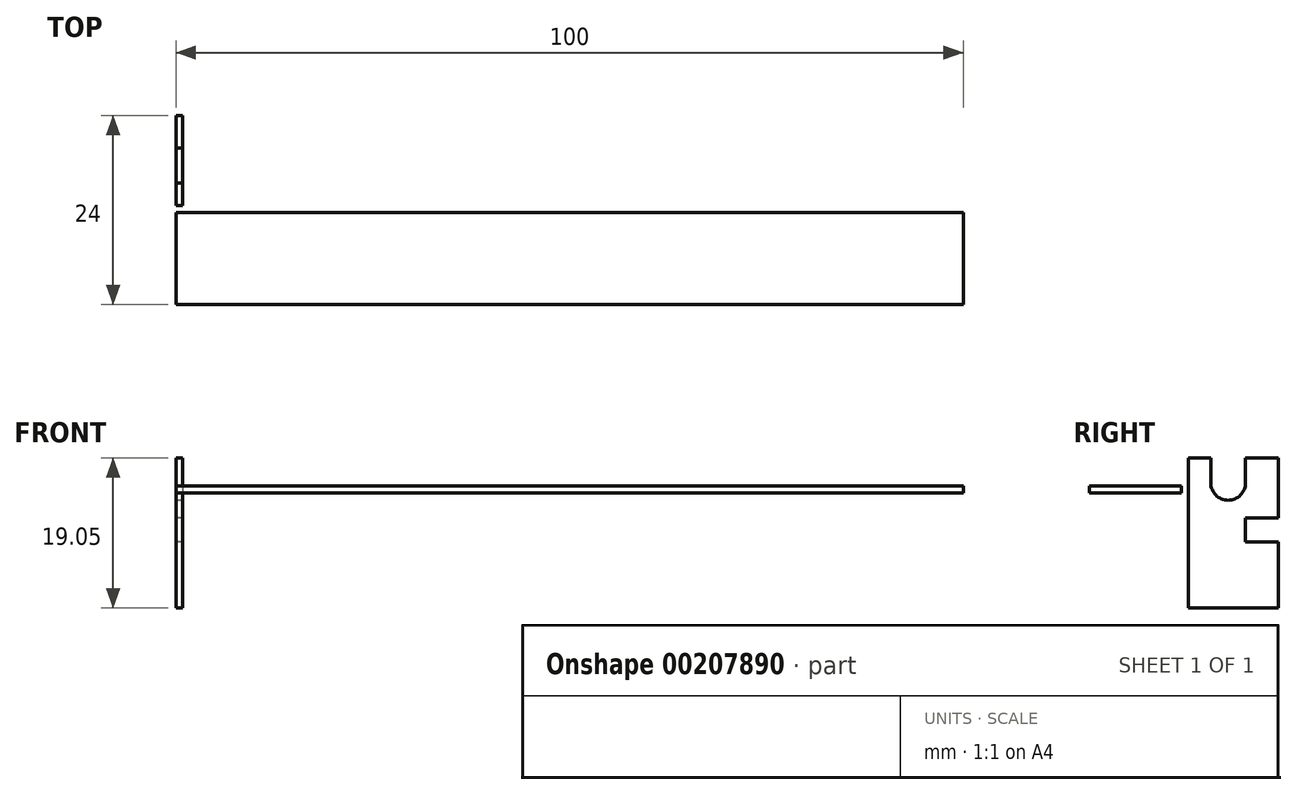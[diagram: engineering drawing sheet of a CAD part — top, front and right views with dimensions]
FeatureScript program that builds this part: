
annotation { "Feature Type Name" : "Feature", "Feature Type Description" : "" }
export const myFeature = defineFeature(function(context is Context, id is Id, definition is map)
    precondition{}
    {
        {
            var Q0;
            Q0=qCreatedBy(makeId("Top.planeOp"),FACE);
            var sketch = newSketch(context, id + "F0", { "sketchPlane" : qUnion([Q0])});
            skLineSegment(sketch, "E0.bottom", {"start": v(-143.4, -300) * mm, "end": v(-114.55, -300) * mm});
            skLineSegment(sketch, "E0.top", {"start": v(-143.4, 0) * mm, "end": v(-114.55, 0) * mm});
            skLineSegment(sketch, "E0.left", {"start": v(-143.4, -300) * mm, "end": v(-143.4, 0) * mm});
            skLineSegment(sketch, "E0.right", {"start": v(-114.55, -300) * mm, "end": v(-114.55, 0) * mm});
            skPoint(sketch, "E1", {"position": v(-3.4, -300) * mm});
            skLineSegment(sketch, "E2", {"start": v(11.76, 1.03) * mm, "end": v(11.76, 1.89) * mm});
            skLineSegment(sketch, "E3", {"start": v(11.76, 1.89) * mm, "end": v(-108.26, 1.89) * mm});
            skLineSegment(sketch, "E4", {"start": v(-108.26, 1.89) * mm, "end": v(-108.26, 13.32) * mm});
            skLineSegment(sketch, "E5", {"start": v(-108.26, 13.32) * mm, "end": v(-109.12, 13.32) * mm});
            skLineSegment(sketch, "E6.bottom", {"start": v(-114.55, -300) * mm, "end": v(-16.15, -300) * mm});
            skLineSegment(sketch, "E6.top", {"start": v(-114.55, 0) * mm, "end": v(-16.15, 0) * mm});
            skLineSegment(sketch, "E6.right", {"start": v(-16.15, -300) * mm, "end": v(-16.15, 0) * mm});
            skLineSegment(sketch, "E7.bottom", {"start": v(-16.15, 0) * mm, "end": v(-7.9, 0) * mm});
            skLineSegment(sketch, "E7.top", {"start": v(-16.15, -15) * mm, "end": v(-7.9, -15) * mm});
            skLineSegment(sketch, "E7.left", {"start": v(-16.15, 0) * mm, "end": v(-16.15, -15) * mm});
            skLineSegment(sketch, "E7.right", {"start": v(-7.9, 0) * mm, "end": v(-7.9, -15) * mm});
            skPoint(sketch, "E8", {"position": v(-7.9, -300) * mm});
            skLineSegment(sketch, "E9.bottom", {"start": v(-16.15, -33.36) * mm, "end": v(-7.9, -33.36) * mm});
            skLineSegment(sketch, "E9.top", {"start": v(-16.15, -41.36) * mm, "end": v(-7.9, -41.36) * mm});
            skLineSegment(sketch, "E9.left", {"start": v(-16.15, -33.36) * mm, "end": v(-16.15, -41.36) * mm});
            skLineSegment(sketch, "E9.right", {"start": v(-7.9, -33.36) * mm, "end": v(-7.9, -41.36) * mm});
            skPoint(sketch, "E10", {"position": v(-3.4, 0) * mm});
            skLineSegment(sketch, "E11", {"start": v(-16.15, -45.01) * mm, "end": v(-3.4, -45.01) * mm});
            skLineSegment(sketch, "E12", {"start": v(-3.4, -45.01) * mm, "end": v(-3.4, -56.21) * mm});
            skLineSegment(sketch, "E13", {"start": v(-3.4, -56.21) * mm, "end": v(-11.8, -56.21) * mm});
            skLineSegment(sketch, "E14", {"start": v(-11.8, -56.21) * mm, "end": v(-11.8, -58.11) * mm});
            skLineSegment(sketch, "E15", {"start": v(-11.8, -58.11) * mm, "end": v(-3.4, -58.11) * mm});
            skLineSegment(sketch, "E16", {"start": v(-3.4, -58.11) * mm, "end": v(-3.4, -129.31) * mm});
            skLineSegment(sketch, "E17", {"start": v(-3.4, -129.31) * mm, "end": v(-16.15, -129.31) * mm});
            skPoint(sketch, "E18", {"position": v(-11.8, -57.16) * mm});
            skArc(sketch, "E19", {"start": v(-14.33, -41.36) * mm, "mid": v(-16.15, -43.19) * mm, "end": v(-14.33, -45.01) * mm});
            skArc(sketch, "E20", {"start": v(-10.85, -56.21) * mm, "mid": v(-11.8, -57.16) * mm, "end": v(-10.85, -58.11) * mm});
            skLineSegment(sketch, "E21", {"start": v(-16.15, -139.06) * mm, "end": v(-11.35, -139.06) * mm});
            skLineSegment(sketch, "E22", {"start": v(-11.35, -139.06) * mm, "end": v(-11.35, -144.76) * mm});
            skLineSegment(sketch, "E23", {"start": v(-11.35, -144.76) * mm, "end": v(-8.77, -144.76) * mm});
            skLineSegment(sketch, "E24", {"start": v(-8.77, -144.76) * mm, "end": v(-6.35, -143.36) * mm});
            skLineSegment(sketch, "E25", {"start": v(-6.35, -143.36) * mm, "end": v(-6.35, -132.06) * mm});
            skLineSegment(sketch, "E26", {"start": v(-6.35, -132.06) * mm, "end": v(-12.38, -132.06) * mm});
            skLineSegment(sketch, "E27", {"start": v(-12.38, -132.06) * mm, "end": v(-12.38, -129.31) * mm});
            skArc(sketch, "E28", {"start": v(-11, -129.31) * mm, "mid": v(-12.38, -130.69) * mm, "end": v(-11, -132.06) * mm});
            skLineSegment(sketch, "E29", {"start": v(-108.26, 1.89) * mm, "end": v(-109.12, 1.89) * mm});
            skLineSegment(sketch, "E30", {"start": v(-109.12, 13.32) * mm, "end": v(-109.12, 1.89) * mm});
            skLineSegment(sketch, "E31", {"start": v(-109.12, 1.03) * mm, "end": v(-109.12, 1.89) * mm});
            skLineSegment(sketch, "E32", {"start": v(-108.26, 1.89) * mm, "end": v(-108.26, 1.03) * mm});
            skLineSegment(sketch, "E33", {"start": v(-108.26, 1.03) * mm, "end": v(-109.12, 1.03) * mm});
            skLineSegment(sketch, "E34", {"start": v(-108.26, 1.03) * mm, "end": v(11.76, 1.03) * mm});
            skPoint(sketch, "E35", {"position": v(0, -57.16) * mm});
            skSolve(sketch);
        }
        {
            var Q0;
            {var subQ7=sQuery(id+"F0.wireOp",EDGE,"E6.bottom");Q0=makeQuery(id+"F0.imprint","IMPRINT",FACE,{"disambiguationData":[TD([[makeQuery(id+"F0.imprint","IMPRINT",EDGE,{"derivedFrom":subQ7}),1.0]])]});}
            var Q1;
            {var subQ5=sQuery(id+"F0.wireOp",EDGE,"E21");Q1=makeQuery(id+"F0.imprint","IMPRINT",FACE,{"disambiguationData":[TD([[makeQuery(id+"F0.imprint","IMPRINT",EDGE,{"derivedFrom":subQ5}),1.0]])]});}
            var Q2;
            {var subQ0=sQuery(id+"F0.wireOp",EDGE,"E27");var subQ1=sQuery(id+"F0.wireOp",EDGE,"E26");var subQ2=makeQuery(id+"F0.imprint","INTERSECT",VERTEX,{"derivedFrom":[subQ1,subQ0]});Q2=makeQuery(id+"F0.imprint","IMPRINT",FACE,{"disambiguationData":[TD([[makeQuery(id+"F0.imprint","IMPRINT",EDGE,{"disambiguationData":[TD([[subQ2,1.0]])],"derivedFrom":subQ1}),-1.0]])]});}
            var Q3;
            {var subQ0=sQuery(id+"F0.wireOp",EDGE,"E27");var subQ1=sQuery(id+"F0.wireOp",EDGE,"E17");var subQ2=makeQuery(id+"F0.imprint","INTERSECT",VERTEX,{"derivedFrom":[subQ1,subQ0]});Q3=makeQuery(id+"F0.imprint","IMPRINT",FACE,{"disambiguationData":[TD([[makeQuery(id+"F0.imprint","IMPRINT",EDGE,{"disambiguationData":[TD([[subQ2,1.0]])],"derivedFrom":subQ1}),1.0]])]});}
            var Q4;
            {var subQ0=sQuery(id+"F0.wireOp",EDGE,"E15");var subQ1=sQuery(id+"F0.wireOp",EDGE,"E14");var subQ2=makeQuery(id+"F0.imprint","INTERSECT",VERTEX,{"derivedFrom":[subQ1,subQ0]});Q4=makeQuery(id+"F0.imprint","IMPRINT",FACE,{"disambiguationData":[TD([[makeQuery(id+"F0.imprint","IMPRINT",EDGE,{"disambiguationData":[TD([[subQ2,1.0]])],"derivedFrom":subQ1}),1.0]])]});}
            var Q5;
            {var subQ0=sQuery(id+"F0.wireOp",EDGE,"E14");var subQ1=sQuery(id+"F0.wireOp",EDGE,"E13");var subQ2=makeQuery(id+"F0.imprint","INTERSECT",VERTEX,{"derivedFrom":[subQ1,subQ0]});Q5=makeQuery(id+"F0.imprint","IMPRINT",FACE,{"disambiguationData":[TD([[makeQuery(id+"F0.imprint","IMPRINT",EDGE,{"disambiguationData":[TD([[subQ2,1.0]])],"derivedFrom":subQ1}),1.0]])]});}
            var Q6;
            {var subQ4=sQuery(id+"F0.wireOp",EDGE,"E12");Q6=makeQuery(id+"F0.imprint","IMPRINT",FACE,{"disambiguationData":[TD([[makeQuery(id+"F0.imprint","IMPRINT",EDGE,{"derivedFrom":subQ4}),-1.0]])]});}
            var Q7;
            {var subQ0=sQuery(id+"F0.wireOp",EDGE,"E11");var subQ1=sQuery(id+"F0.wireOp",EDGE,"E6.right");var subQ2=makeQuery(id+"F0.imprint","INTERSECT",VERTEX,{"derivedFrom":[subQ1,subQ0]});Q7=makeQuery(id+"F0.imprint","IMPRINT",FACE,{"disambiguationData":[TD([[makeQuery(id+"F0.imprint","IMPRINT",EDGE,{"disambiguationData":[TD([[subQ2,-1.0]])],"derivedFrom":subQ1}),-1.0]])]});}
            var Q8;
            {var subQ0=sQuery(id+"F0.wireOp",EDGE,"E9.top");var subQ3=sQuery(id+"F0.wireOp",EDGE,"E19");var subQ5=makeQuery(id+"F0.imprint","INTERSECT",VERTEX,{"derivedFrom":[subQ0,subQ3]});Q8=makeQuery(id+"F0.imprint","IMPRINT",FACE,{"disambiguationData":[TD([[makeQuery(id+"F0.imprint","IMPRINT",EDGE,{"disambiguationData":[TD([[subQ5,-1.0]])],"derivedFrom":subQ3}),-1.0]])]});}
            var Q9;
            Q9=makeQuery(id+"F0.imprint","IMPRINT",FACE,{"disambiguationData":[TD([[makeQuery(id+"F0.imprint","IMPRINT",EDGE,{"derivedFrom":sQuery(id+"F0.wireOp",EDGE,"E9.bottom")}),-1.0]])]});
            var Q10;
            Q10=makeQuery(id+"F0.imprint","IMPRINT",FACE,{"disambiguationData":[TD([[makeQuery(id+"F0.imprint","IMPRINT",EDGE,{"derivedFrom":sQuery(id+"F0.wireOp",EDGE,"E7.bottom")}),-1.0]])]});
            extrude(context, id + "F1", {"entities" : qUnion([Q0, Q1, Q2, Q3, Q4, Q5, Q6, Q7, Q8, Q9, Q10]), "endBound" : BoundingType.SYMMETRIC, "depth" : 1.57 * mm});
        }
        {
            var Q0;
            Q0=makeQuery(id+"F0.imprint","IMPRINT",FACE,{"disambiguationData":[TD([[makeQuery(id+"F0.imprint","IMPRINT",EDGE,{"derivedFrom":sQuery(id+"F0.wireOp",EDGE,"E2")}),1.0]])]});
            extrude(context, id + "F2", {"entities" : qUnion([Q0]), "endBound" : BoundingType.SYMMETRIC, "depth" : 40 * mm});
        }
        {
            var Q0;
            Q0=makeQuery(id+"F2.opExtrude","SWEPT_FACE",FACE,{"disambiguationData":[OSD([sQuery(id+"F0.wireOp",EDGE,"E3")])]});
            var sketch = newSketch(context, id + "F3", { "sketchPlane" : qUnion([Q0])});
            skLineSegment(sketch, "E36", {"start": v(-4.49, -2.06) * mm, "end": v(-11.76, -2.06) * mm});
            skLineSegment(sketch, "E37", {"start": v(-11.76, -2.06) * mm, "end": v(-11.76, -12.25) * mm});
            skLineSegment(sketch, "E38", {"start": v(-11.76, -12.25) * mm, "end": v(-4.49, -12.25) * mm});
            skLineSegment(sketch, "E39", {"start": v(-4.49, -12.25) * mm, "end": v(-0.38, -16.36) * mm});
            skLineSegment(sketch, "E40", {"start": v(-0.38, -16.36) * mm, "end": v(101.78, -16.36) * mm});
            skLineSegment(sketch, "E41", {"start": v(108.26, -13.82) * mm, "end": v(108.26, 5.23) * mm});
            skLineSegment(sketch, "E42", {"start": v(108.26, 5.23) * mm, "end": v(105.34, 5.23) * mm});
            skLineSegment(sketch, "E43", {"start": v(103.7, 2.06) * mm, "end": v(-0.37, 2.05) * mm});
            skLineSegment(sketch, "E44", {"start": v(-0.37, 2.05) * mm, "end": v(-4.49, -2.06) * mm});
            skLineSegment(sketch, "E45.bottom", {"start": v(7.9, 0.78) * mm, "end": v(114.55, 0.78) * mm});
            skLineSegment(sketch, "E45.top", {"start": v(7.9, -0.78) * mm, "end": v(114.55, -0.78) * mm});
            skLineSegment(sketch, "E45.left", {"start": v(7.9, 0.78) * mm, "end": v(7.9, -0.78) * mm});
            skLineSegment(sketch, "E45.right", {"start": v(114.55, 0.78) * mm, "end": v(114.55, -0.78) * mm});
            skPoint(sketch, "E46", {"position": v(7.9, 0) * mm});
            skLineSegment(sketch, "E47", {"start": v(108.26, -13.82) * mm, "end": v(104.32, -13.82) * mm});
            skLineSegment(sketch, "E48", {"start": v(104.32, -13.82) * mm, "end": v(101.78, -16.36) * mm});
            skLineSegment(sketch, "E49", {"start": v(103.7, 2.05) * mm, "end": v(103.7, 3.59) * mm});
            skLineSegment(sketch, "E50", {"start": v(103.7, 3.59) * mm, "end": v(105.34, 5.23) * mm});
            skSolve(sketch);
        }
        {
            var Q0;
            Q0=makeQuery(id+"F3.imprint","IMPRINT",FACE,{"disambiguationData":[TD([[makeQuery(id+"F3.imprint","IMPRINT",EDGE,{"derivedFrom":sQuery(id+"F3.wireOp",EDGE,"E36")}),1.0]])]});
            var Q1;
            {var subQ5=sQuery(id+"F3.wireOp",EDGE,"E45.left");Q1=makeQuery(id+"F3.imprint","IMPRINT",FACE,{"disambiguationData":[TD([[makeQuery(id+"F3.imprint","IMPRINT",EDGE,{"derivedFrom":subQ5}),1.0]])]});}
            extrude(context, id + "F4", {"entities" : qUnion([Q0, Q1]), "operationType" : NewBodyOperationType.INTERSECT, "oppositeDirection" : true, "depth" : 0.86 * mm});
        }
        {
            var Q0;
            Q0=makeQuery(id+"F0.imprint","IMPRINT",FACE,{"disambiguationData":[TD([[makeQuery(id+"F0.imprint","IMPRINT",EDGE,{"derivedFrom":sQuery(id+"F0.wireOp",EDGE,"E29")}),1.0]])]});
            var Q1;
            Q1=makeQuery(id+"F0.imprint","IMPRINT",FACE,{"disambiguationData":[TD([[makeQuery(id+"F0.imprint","IMPRINT",EDGE,{"derivedFrom":sQuery(id+"F0.wireOp",EDGE,"E4")}),1.0]])]});
            extrude(context, id + "F5", {"entities" : qUnion([Q0, Q1]), "operationType" : NewBodyOperationType.ADD, "endBound" : BoundingType.SYMMETRIC, "depth" : 30 * mm});
        }
        {
            var Q0;
            Q0=makeQuery(id+"F5.opExtrude","SWEPT_FACE",FACE,{"disambiguationData":[OSD([sQuery(id+"F0.wireOp",EDGE,"E30"),sQuery(id+"F0.wireOp",EDGE,"E31")])]});
            var sketch = newSketch(context, id + "F6", { "sketchPlane" : qUnion([Q0])});
            skLineSegment(sketch, "E51", {"start": v(-13.32, 5.23) * mm, "end": v(-13.32, -2.4) * mm});
            skLineSegment(sketch, "E52", {"start": v(-13.32, -2.4) * mm, "end": v(-9.13, -2.4) * mm});
            skLineSegment(sketch, "E53", {"start": v(-9.13, -2.4) * mm, "end": v(-9.13, -5.44) * mm});
            skLineSegment(sketch, "E54", {"start": v(-9.13, -5.44) * mm, "end": v(-13.32, -5.44) * mm});
            skLineSegment(sketch, "E55", {"start": v(-13.32, -5.44) * mm, "end": v(-13.32, -13.82) * mm});
            skLineSegment(sketch, "E56", {"start": v(-13.32, -13.82) * mm, "end": v(-1.03, -13.82) * mm});
            skLineSegment(sketch, "E57", {"start": v(-1.03, -13.82) * mm, "end": v(-1.03, 5.23) * mm});
            skLineSegment(sketch, "E58", {"start": v(-4.76, 5.23) * mm, "end": v(-4.76, -0.15) * mm});
            skLineSegment(sketch, "E59", {"start": v(-4.76, -0.15) * mm, "end": v(-9.18, -0.15) * mm});
            skLineSegment(sketch, "E60", {"start": v(-9.18, -0.15) * mm, "end": v(-9.18, 5.23) * mm});
            skLineSegment(sketch, "E61", {"start": v(-9.18, 5.23) * mm, "end": v(-13.32, 5.23) * mm});
            skPoint(sketch, "E62", {"position": v(-13.32, -16.36) * mm});
            skArc(sketch, "E63", {"start": v(-9.18, 2.06) * mm, "mid": v(-6.97, -0.15) * mm, "end": v(-4.76, 2.06) * mm});
            skLineSegment(sketch, "E64.bottom", {"start": v(0, 0.78) * mm, "end": v(300, 0.78) * mm});
            skLineSegment(sketch, "E64.top", {"start": v(0, -0.78) * mm, "end": v(300, -0.78) * mm});
            skLineSegment(sketch, "E64.left", {"start": v(0, 0.78) * mm, "end": v(0, -0.78) * mm});
            skLineSegment(sketch, "E64.right", {"start": v(300, 0.78) * mm, "end": v(300, -0.78) * mm});
            skPoint(sketch, "E65", {"position": v(0, 0) * mm});
            skLineSegment(sketch, "E66.bottom", {"start": v(10.68, 1.65) * mm, "end": v(-1.03, 1.65) * mm});
            skLineSegment(sketch, "E66.top", {"start": v(10.68, 0.79) * mm, "end": v(-1.03, 0.79) * mm});
            skLineSegment(sketch, "E66.left", {"start": v(10.68, 1.65) * mm, "end": v(10.68, 0.79) * mm});
            skLineSegment(sketch, "E66.right", {"start": v(-1.03, 1.65) * mm, "end": v(-1.03, 0.79) * mm});
            skLineSegment(sketch, "E67", {"start": v(-1.89, 5.23) * mm, "end": v(-1.89, -13.82) * mm});
            skLineSegment(sketch, "E68", {"start": v(-4.76, 5.22) * mm, "end": v(-1.89, 5.22) * mm});
            skLineSegment(sketch, "E69", {"start": v(-1.89, 5.23) * mm, "end": v(-1.03, 5.23) * mm});
            skSolve(sketch);
        }
        {
            var Q0;
            Q0=makeQuery(id+"F6.imprint","IMPRINT",FACE,{"disambiguationData":[TD([[makeQuery(id+"F6.imprint","IMPRINT",EDGE,{"derivedFrom":sQuery(id+"F6.wireOp",EDGE,"E51")}),1.0]])]});
            var Q1;
            {var subQ0=sQuery(id+"F6.wireOp",EDGE,"E60");var subQ1=sQuery(id+"F6.wireOp",EDGE,"E59");var subQ2=makeQuery(id+"F6.imprint","INTERSECT",VERTEX,{"derivedFrom":[subQ1,subQ0]});Q1=makeQuery(id+"F6.imprint","IMPRINT",FACE,{"disambiguationData":[TD([[makeQuery(id+"F6.imprint","IMPRINT",EDGE,{"disambiguationData":[TD([[subQ2,1.0]])],"derivedFrom":subQ1}),-1.0]])]});}
            var Q2;
            {var subQ0=sQuery(id+"F6.wireOp",EDGE,"E59");var subQ1=sQuery(id+"F6.wireOp",EDGE,"E58");var subQ2=makeQuery(id+"F6.imprint","INTERSECT",VERTEX,{"derivedFrom":[subQ1,subQ0]});Q2=makeQuery(id+"F6.imprint","IMPRINT",FACE,{"disambiguationData":[TD([[makeQuery(id+"F6.imprint","IMPRINT",EDGE,{"disambiguationData":[TD([[subQ2,1.0]])],"derivedFrom":subQ1}),-1.0]])]});}
            var Q3;
            {var subQ4=sQuery(id+"F6.wireOp",EDGE,"E66.right");Q3=makeQuery(id+"F6.imprint","IMPRINT",FACE,{"disambiguationData":[TD([[makeQuery(id+"F6.imprint","IMPRINT",EDGE,{"derivedFrom":subQ4}),-1.0]])]});}
            extrude(context, id + "F7", {"entities" : qUnion([Q0, Q1, Q2, Q3]), "operationType" : NewBodyOperationType.INTERSECT, "oppositeDirection" : true, "depth" : 0.86 * mm});
        }
        {
            var Q0;
            Q0=makeQuery(id+"F6.imprint","IMPRINT",FACE,{"disambiguationData":[TD([[makeQuery(id+"F6.imprint","IMPRINT",EDGE,{"derivedFrom":sQuery(id+"F6.wireOp",EDGE,"E66.bottom")}),1.0]])]});
            extrude(context, id + "F8", {"entities" : qUnion([Q0]), "operationType" : NewBodyOperationType.ADD, "oppositeDirection" : true, "depth" : 100 * mm});
        }
    });
